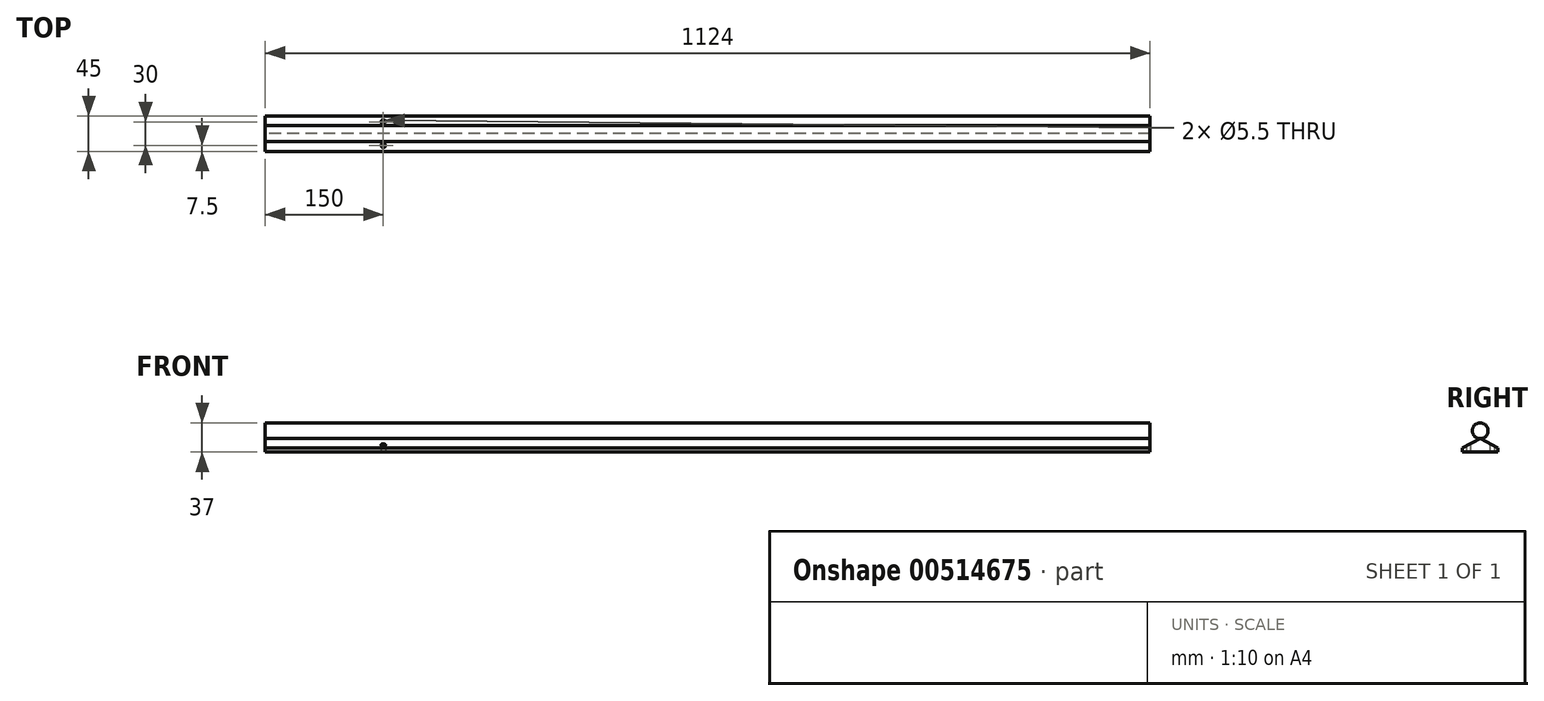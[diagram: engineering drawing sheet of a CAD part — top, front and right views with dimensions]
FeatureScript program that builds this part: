
annotation { "Feature Type Name" : "Feature", "Feature Type Description" : "" }
export const myFeature = defineFeature(function(context is Context, id is Id, definition is map)
    precondition{}
    {
        {
            var Q0;
            Q0=qCreatedBy(makeId("Right.planeOp"),FACE);
            var sketch = newSketch(context, id + "F0", { "sketchPlane" : qUnion([Q0])});
            skLineSegment(sketch, "E0.bottom", {"start": v(0, 0) * mm, "end": v(-45, 0) * mm});
            skLineSegment(sketch, "E0.top", {"start": v(0, 5) * mm, "end": v(-45, 5) * mm});
            skLineSegment(sketch, "E0.left", {"start": v(0, 0) * mm, "end": v(0, 5) * mm});
            skLineSegment(sketch, "E0.right", {"start": v(-45, 0) * mm, "end": v(-45, 5) * mm});
            skCircle(sketch, "E1", {"center": v(-22.5, 27) * mm, "radius": 10 * mm});
            skPoint(sketch, "E2", {"position": v(-22.5, 5) * mm});
            skLineSegment(sketch, "E3", {"start": v(-22.5, 17) * mm, "end": v(-45, 5) * mm});
            skLineSegment(sketch, "E4", {"start": v(-22.5, 17) * mm, "end": v(0, 5) * mm});
            skSolve(sketch);
        }
        {
            var Q0;
            Q0=makeQuery(id+"F0.imprint","IMPRINT",FACE,{"disambiguationData":[TD([[makeQuery(id+"F0.imprint","IMPRINT",EDGE,{"derivedFrom":sQuery(id+"F0.wireOp",EDGE,"E0.bottom")}),-1.0]])]});
            var Q1;
            Q1=makeQuery(id+"F0.imprint","IMPRINT",FACE,{"disambiguationData":[TD([[makeQuery(id+"F0.imprint","IMPRINT",EDGE,{"derivedFrom":sQuery(id+"F0.wireOp",EDGE,"E0.top")}),-1.0]])]});
            var Q2;
            Q2=makeQuery(id+"F0.imprint","IMPRINT",FACE,{"disambiguationData":[TD([[makeQuery(id+"F0.imprint","IMPRINT",EDGE,{"derivedFrom":sQuery(id+"F0.wireOp",EDGE,"E1")}),1.0]])]});
            extrude(context, id + "F1", {"entities" : qUnion([Q0, Q1, Q2]), "depth" : 1124 * mm, "offsetDistance" : 25 * mm});
        }
        {
            var Q0;
            Q0=makeQuery(id+"F1.opExtrude","SWEPT_FACE",FACE,{"disambiguationData":[OSD([sQuery(id+"F0.wireOp",EDGE,"E0.bottom")])]});
            var sketch = newSketch(context, id + "F2", { "sketchPlane" : qUnion([Q0])});
            skPoint(sketch, "E5", {"position": v(150, 37.5) * mm});
            skPoint(sketch, "E6", {"position": v(150, 7.5) * mm});
            skSolve(sketch);
        }
        {
            var Q0;
            Q0=sQuery(id+"F2.wireOp",VERTEX,"E5");
            var Q1;
            Q1=sQuery(id+"F2.wireOp",VERTEX,"E6");
            var Q2;
            Q2=makeQuery(id+"F1.opExtrude","SWEPT_BODY",BODY,{"disambiguationData":[OSD([sQuery(id+"F0.wireOp",EDGE,"E0.bottom"),sQuery(id+"F0.wireOp",EDGE,"E0.left"),sQuery(id+"F0.wireOp",EDGE,"E0.right"),sQuery(id+"F0.wireOp",EDGE,"E3"),sQuery(id+"F0.wireOp",EDGE,"E4")])]});
            hole(context, id + "F3", {"style" : HoleStyle.SIMPLE, "endStyle" : HoleEndStyle.THROUGH, "holeDiameter" : 5.5 * mm, "isTappedThrough" : true, "tappedDepth" : 12 * mm, "tapClearance" : 3, "locations" : qUnion([Q0, Q1]), "scope" : qUnion([Q2])});
        }
    });
